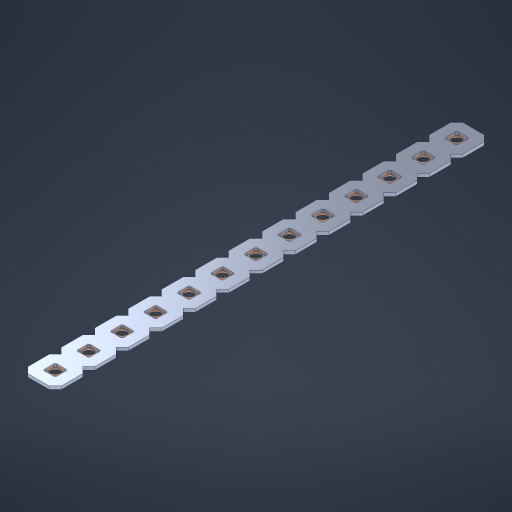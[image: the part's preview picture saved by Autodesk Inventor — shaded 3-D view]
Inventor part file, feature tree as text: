
AUTODESK INVENTOR PART (.ipt)
format: ipt  version: 2023 (Build 270158000, 158)  size: 429,568 bytes
history: native  units: in
note: dims shown in document units (in); Inventor stores cm internally (conversion verified against a paired STEP export)
features: other x14, extrude x12, sketch x2, pattern_linear x1
ambient origin geometry x8: Origin, YZ Plane, XZ Plane, XY Plane, X Axis, Y Axis, Z Axis, Center Point
bodies: Solid1 (feature_tree), Body (feature_tree)
feature tree (29):
  pattern_linear  "Rectangular Pattern1"  Spacing1=0.09in  [1 undecoded]
  sketch  "Sketch1"  dims[d1=0.5in]
  sketch  "Sketch2"  dims[d2=0.182in d3=0.09in d4=0.09in d5=0.09in d6=0.09in d7=0.09in d8=0.09in d9=0.09in d10=0.09in d11=0.02in d13=0.0in d14=0.172in d15=0.0625in d16=0.0in d19=0.5in d22=0.5in]
  other  "Srf1"
  other  "Srf126"
  other  "Srf127"
  other  "Srf128"
  other  "Srf129"
  other  "Srf130"
  other  "Srf131"
  other  "Srf250"
  other  "Srf251"
  other  "Srf252"
  other  "Srf253"
  other  "Srf254"
  other  "Srf255"
  other  "Circle"
  extrude  "ExtrusionSrf126"  Depth=0.09in
  extrude  "ExtrusionSrf127"  Depth=0.09in
  extrude  "ExtrusionSrf128"  Depth=0.09in
  extrude  "ExtrusionSrf129"  Depth=0.09in
  extrude  "ExtrusionSrf130"  Depth=0.09in
  extrude  "ExtrusionSrf131"  Depth=0.09in
  extrude  "ExtrusionSrf250"  Depth=0.09in
  extrude  "ExtrusionSrf251"  Depth=0.02in
  extrude  "ExtrusionSrf252"  TaperAngle=0.0deg  [1 undecoded]
  extrude  "ExtrusionSrf253"  Depth=0.5in
  extrude  "ExtrusionSrf254"  Depth=0.5in TaperAngle=0.0deg
  extrude  "ExtrusionSrf255"  Depth=0.5in
note: 2 required parameter values undecoded (feature->parameter linkage not recoverable at this tier; creation-order binding heuristic only, values carry confidence <= 0.55)
